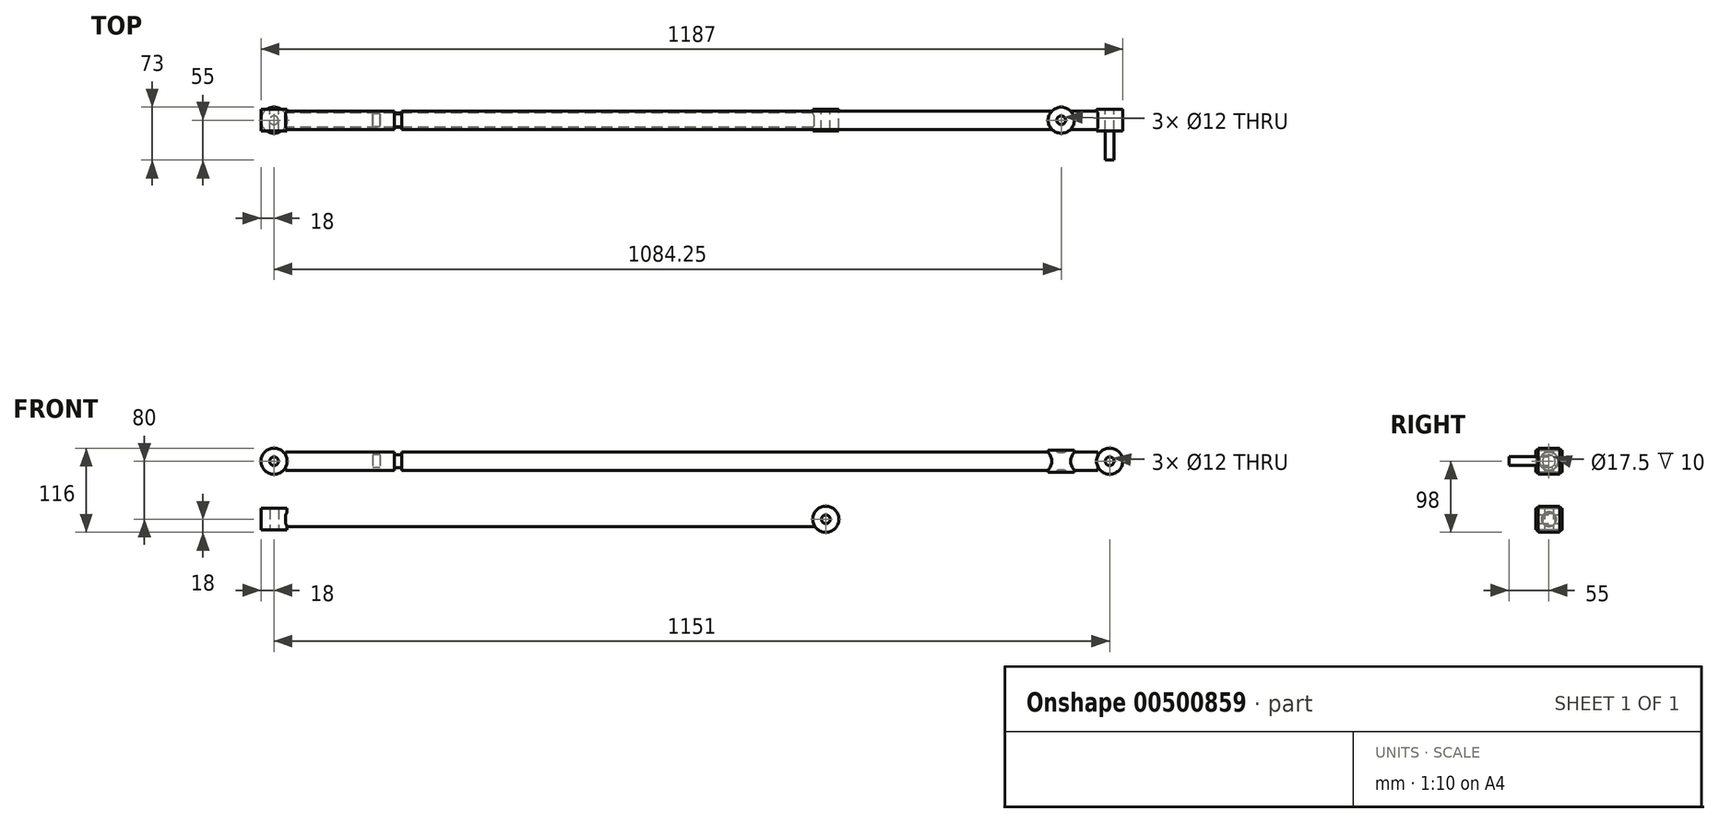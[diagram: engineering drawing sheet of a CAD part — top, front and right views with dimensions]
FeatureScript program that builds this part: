
annotation { "Feature Type Name" : "Feature", "Feature Type Description" : "" }
export const myFeature = defineFeature(function(context is Context, id is Id, definition is map)
    precondition{}
    {
        {
            var Q0;
            Q0=qCreatedBy(makeId("Front.planeOp"),FACE);
            var sketch = newSketch(context, id + "F0", { "sketchPlane" : qUnion([Q0])});
            skLineSegment(sketch, "E0", {"start": v(0, 0) * mm, "end": v(16, 0) * mm});
            skLineSegment(sketch, "E1", {"start": v(16, 0) * mm, "end": v(1135, 0) * mm});
            skLineSegment(sketch, "E2", {"start": v(1135, 0) * mm, "end": v(1135, 12.75) * mm});
            skLineSegment(sketch, "E3", {"start": v(1135, 12.75) * mm, "end": v(16, 12.75) * mm});
            skLineSegment(sketch, "E4", {"start": v(16, 12.75) * mm, "end": v(16, 0) * mm});
            skPoint(sketch, "E5", {"position": v(16, 12.75) * mm});
            skPoint(sketch, "E6", {"position": v(166, 12.75) * mm});
            skPoint(sketch, "E7", {"position": v(166, 0) * mm});
            skLineSegment(sketch, "E8", {"start": v(166, 12.75) * mm, "end": v(166, 8.75) * mm});
            skLineSegment(sketch, "E9", {"start": v(166, 8.75) * mm, "end": v(146, 8.75) * mm});
            skLineSegment(sketch, "E10", {"start": v(146, 8.75) * mm, "end": v(146, 0) * mm});
            skLineSegment(sketch, "E11", {"start": v(166, 0) * mm, "end": v(156, 0) * mm});
            skLineSegment(sketch, "E12", {"start": v(166, 8.75) * mm, "end": v(176, 8.75) * mm});
            skLineSegment(sketch, "E13", {"start": v(176, 8.75) * mm, "end": v(176, 12.75) * mm});
            skLineSegment(sketch, "E14", {"start": v(146, 8.75) * mm, "end": v(136, 8.75) * mm});
            skLineSegment(sketch, "E15", {"start": v(136, 8.75) * mm, "end": v(136, 0) * mm});
            skSolve(sketch);
        }
        {
            var Q0;
            {var subQ1=sQuery(id+"F0.wireOp",EDGE,"E4");Q0=makeQuery(id+"F0.imprint","IMPRINT",FACE,{"disambiguationData":[TD([[makeQuery(id+"F0.imprint","IMPRINT",EDGE,{"derivedFrom":subQ1}),1.0]])]});}
            var Q1;
            {var subQ1=sQuery(id+"F0.wireOp",EDGE,"E2");Q1=makeQuery(id+"F0.imprint","IMPRINT",FACE,{"disambiguationData":[TD([[makeQuery(id+"F0.imprint","IMPRINT",EDGE,{"derivedFrom":subQ1}),1.0]])]});}
            var Q2;
            Q2=sQuery(id+"F0.wireOp",EDGE,"E1");
            revolve(context, id + "F1", {"entities" : qUnion([Q0, Q1]), "axis" : qUnion([Q2]), "revolveType" : RevolveType.FULL});
        }
        {
            var Q0;
            Q0=qCreatedBy(makeId("Front.planeOp"),FACE);
            var sketch = newSketch(context, id + "F2", { "sketchPlane" : qUnion([Q0])});
            skCircle(sketch, "E16", {"center": v(0, 0) * mm, "radius": 18 * mm});
            skCircle(sketch, "E17", {"center": v(0, 0) * mm, "radius": 6 * mm});
            skPoint(sketch, "E18", {"position": v(1151, 0) * mm});
            skCircle(sketch, "E19", {"center": v(1151, 0) * mm, "radius": 18 * mm});
            skCircle(sketch, "E20", {"center": v(1151, 0) * mm, "radius": 6 * mm});
            skPoint(sketch, "E21", {"position": v(1084.25, 0) * mm});
            skCircle(sketch, "E22", {"center": v(1084.25, 0) * mm, "radius": 18 * mm, "construction": true});
            skCircle(sketch, "E23", {"center": v(1084.25, 0) * mm, "radius": 6 * mm, "construction": true});
            skSolve(sketch);
        }
        {
            var Q0;
            Q0=qSketchRegion(id+"F2",true);
            extrude(context, id + "F3", {"entities" : qUnion([Q0]), "operationType" : NewBodyOperationType.ADD, "endBound" : BoundingType.SYMMETRIC, "depth" : 30 * mm});
        }
        {
            var Q0;
            Q0=makeQuery(id+"F3.opExtrude","CAP_FACE",FACE,{"disambiguationData":[OSD([sQuery(id+"F2.wireOp",EDGE,"E19"),sQuery(id+"F2.wireOp",EDGE,"E20")])],"isStart":false});
            var sketch = newSketch(context, id + "F4", { "sketchPlane" : qUnion([Q0])});
            skCircle(sketch, "E24.0", {"center": v(1151, 0) * mm, "radius": 6 * mm});
            skSolve(sketch);
        }
        {
            var Q0;
            Q0=qSketchRegion(id+"F4",true);
            extrude(context, id + "F5", {"entities" : qUnion([Q0]), "depth" : 40 * mm});
        }
        {
            var Q0;
            Q0=qCreatedBy(makeId("Front.planeOp"),FACE);
            var sketch = newSketch(context, id + "F6", { "sketchPlane" : qUnion([Q0])});
            skPoint(sketch, "E25", {"position": v(0, -80) * mm});
            skPoint(sketch, "E26", {"position": v(16, -80) * mm});
            skLineSegment(sketch, "E27", {"start": v(16, -80) * mm, "end": v(744, -80) * mm});
            skLineSegment(sketch, "E28", {"start": v(16, -80) * mm, "end": v(16, -70) * mm});
            skLineSegment(sketch, "E29", {"start": v(16, -70) * mm, "end": v(744, -70) * mm});
            skLineSegment(sketch, "E30", {"start": v(744, -70) * mm, "end": v(744, -80) * mm});
            skSolve(sketch);
        }
        {
            var Q0;
            Q0=qSketchRegion(id+"F6",true);
            var Q1;
            Q1=sQuery(id+"F6.wireOp",EDGE,"E27");
            revolve(context, id + "F7", {"entities" : qUnion([Q0]), "axis" : qUnion([Q1]), "revolveType" : RevolveType.FULL});
        }
        {
            var Q0;
            Q0=qCreatedBy(makeId("Front.planeOp"),FACE);
            var sketch = newSketch(context, id + "F8", { "sketchPlane" : qUnion([Q0])});
            skPoint(sketch, "E31", {"position": v(0, -80) * mm});
            skCircle(sketch, "E32", {"center": v(0, -80) * mm, "radius": 18 * mm, "construction": true});
            skCircle(sketch, "E33", {"center": v(0, -80) * mm, "radius": 6 * mm, "construction": true});
            skPoint(sketch, "E34", {"position": v(760, -80) * mm});
            skCircle(sketch, "E35", {"center": v(760, -80) * mm, "radius": 18 * mm});
            skCircle(sketch, "E36", {"center": v(760, -80) * mm, "radius": 6 * mm});
            skSolve(sketch);
        }
        {
            var Q0;
            Q0=qSketchRegion(id+"F8",true);
            extrude(context, id + "F9", {"entities" : qUnion([Q0]), "operationType" : NewBodyOperationType.ADD, "endBound" : BoundingType.SYMMETRIC, "depth" : 30 * mm});
        }
        {
            var Q0;
            Q0=qCreatedBy(makeId("Top.planeOp"),FACE);
            cPlane(context, id + "F10", {"entities" : qUnion([Q0]), "cplaneType" : CPlaneType.OFFSET, "offset" : 80 * mm, "oppositeDirection" : true, "width" : 150 * mm, "height" : 150 * mm});
        }
        {
            var Q0;
            Q0=qCreatedBy(id+"F10.planeOp",FACE);
            var sketch = newSketch(context, id + "F11", { "sketchPlane" : qUnion([Q0])});
            skCircle(sketch, "E37", {"center": v(0, 0) * mm, "radius": 18 * mm});
            skCircle(sketch, "E38", {"center": v(0, 0) * mm, "radius": 6 * mm});
            skSolve(sketch);
        }
        {
            var Q0;
            Q0=qSketchRegion(id+"F11",true);
            extrude(context, id + "F12", {"entities" : qUnion([Q0]), "operationType" : NewBodyOperationType.ADD, "endBound" : BoundingType.SYMMETRIC, "depth" : 30 * mm});
        }
        {
            var Q0;
            Q0=qCreatedBy(makeId("Top.planeOp"),FACE);
            var sketch = newSketch(context, id + "F13", { "sketchPlane" : qUnion([Q0])});
            skLineSegment(sketch, "E39.0", {"start": v(1157, -55) * mm, "end": v(1145, -55) * mm});
            skPoint(sketch, "E40", {"position": v(1084.25, 0) * mm});
            skPoint(sketch, "E41", {"position": v(1151, -55) * mm});
            skCircle(sketch, "E42", {"center": v(1084.25, 0) * mm, "radius": 18 * mm});
            skCircle(sketch, "E43", {"center": v(1084.25, 0) * mm, "radius": 6 * mm});
            skSolve(sketch);
        }
        {
            var Q0;
            Q0=qSketchRegion(id+"F13",true);
            extrude(context, id + "F14", {"entities" : qUnion([Q0]), "operationType" : NewBodyOperationType.ADD, "endBound" : BoundingType.SYMMETRIC, "depth" : 30 * mm});
        }
    });
